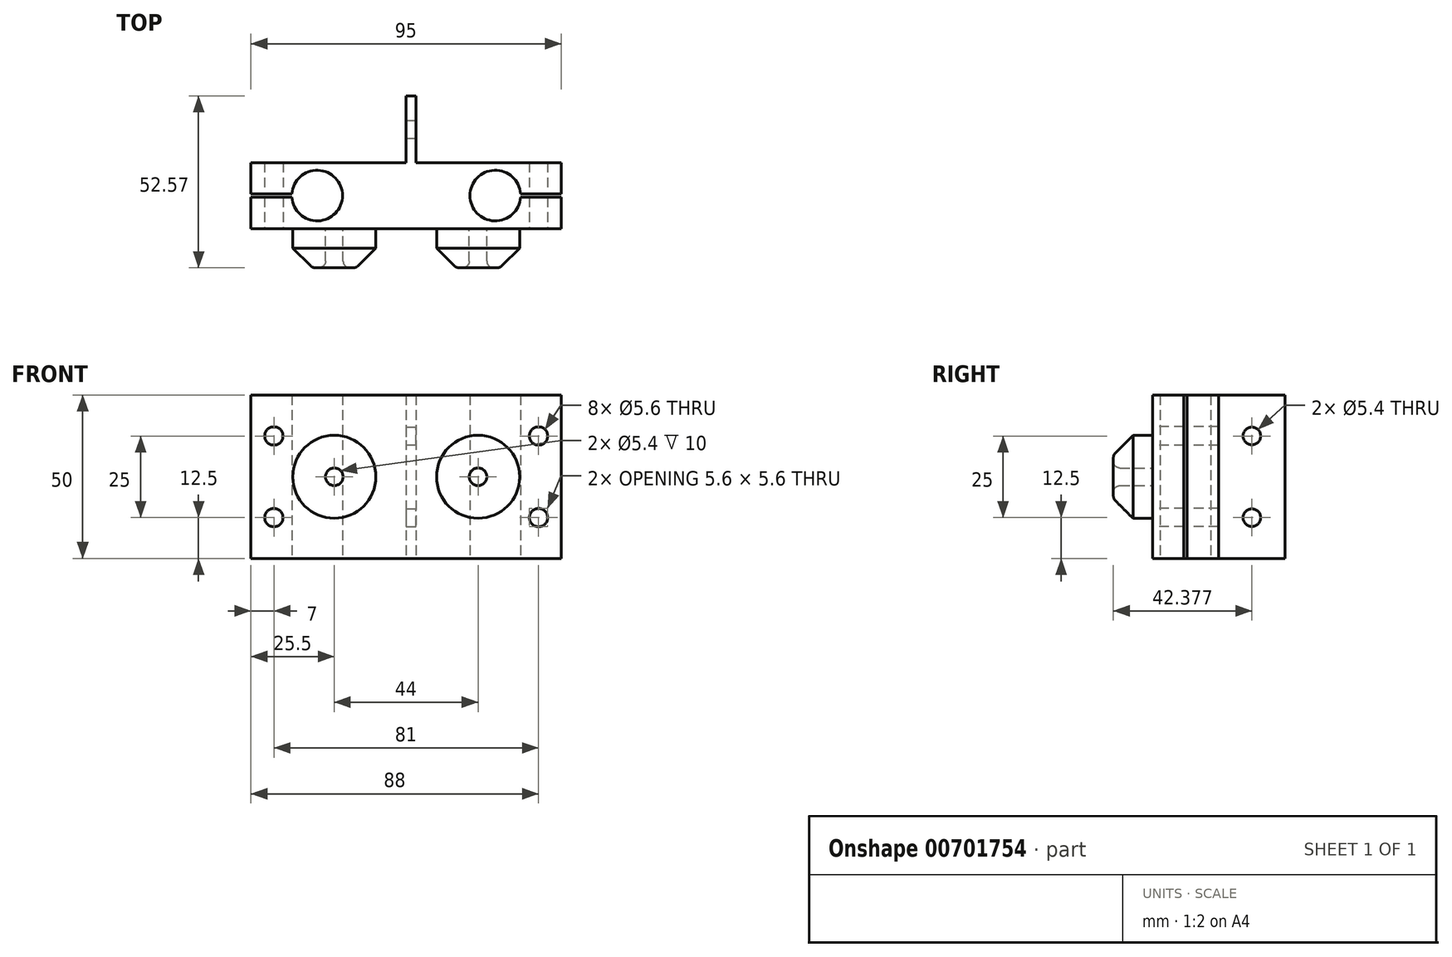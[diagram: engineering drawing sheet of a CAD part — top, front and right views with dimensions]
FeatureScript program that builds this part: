
annotation { "Feature Type Name" : "Feature", "Feature Type Description" : "" }
export const myFeature = defineFeature(function(context is Context, id is Id, definition is map)
    precondition{}
    {
        {
            var Q0;
            Q0=qCreatedBy(makeId("Top.planeOp"),FACE);
            var sketch = newSketch(context, id + "F0", { "sketchPlane" : qUnion([Q0])});
            skCircle(sketch, "E0", {"center": v(-27.25, 0) * mm, "radius": 7.75 * mm});
            skCircle(sketch, "E1", {"center": v(27.25, 0) * mm, "radius": 7.75 * mm});
            skLineSegment(sketch, "E2.bottom", {"start": v(47.5, 10.1) * mm, "end": v(-47.5, 10.1) * mm});
            skLineSegment(sketch, "E2.top", {"start": v(47.5, -10.1) * mm, "end": v(-47.5, -10.1) * mm});
            skLineSegment(sketch, "E2.left", {"start": v(47.5, 10.1) * mm, "end": v(47.5, 0.5) * mm});
            skLineSegment(sketch, "E2.right", {"start": v(-47.5, 10.1) * mm, "end": v(-47.5, 0.5) * mm});
            skPoint(sketch, "E2.middle", {"position": v(0, 0) * mm});
            skLineSegment(sketch, "E3", {"start": v(0, 10.1) * mm, "end": v(0, 36.66) * mm, "construction": true});
            skLineSegment(sketch, "E4.bottom", {"start": v(0, 10.1) * mm, "end": v(-3, 10.1) * mm});
            skLineSegment(sketch, "E4.top", {"start": v(0, 30.48) * mm, "end": v(-3, 30.48) * mm});
            skLineSegment(sketch, "E4.left", {"start": v(0, 10.1) * mm, "end": v(0, 30.48) * mm});
            skLineSegment(sketch, "E4.right", {"start": v(-3, 10.1) * mm, "end": v(-3, 30.48) * mm});
            skLineSegment(sketch, "E5.bottom", {"start": v(-4.5, 10.1) * mm, "end": v(-9.5, 10.1) * mm});
            skLineSegment(sketch, "E5.top", {"start": v(-4.5, 30.48) * mm, "end": v(-9.5, 30.48) * mm});
            skLineSegment(sketch, "E5.left", {"start": v(-4.5, 10.1) * mm, "end": v(-4.5, 30.48) * mm});
            skLineSegment(sketch, "E5.right", {"start": v(-9.5, 10.1) * mm, "end": v(-9.5, 30.48) * mm});
            skLineSegment(sketch, "E6.MirrorCS", {"start": v(0, 30.48) * mm, "end": v(3, 30.48) * mm});
            skLineSegment(sketch, "E7.MirrorCS", {"start": v(3, 10.1) * mm, "end": v(3, 30.48) * mm});
            skLineSegment(sketch, "E8.MirrorCS", {"start": v(4.5, 30.48) * mm, "end": v(9.5, 30.48) * mm});
            skLineSegment(sketch, "E9.MirrorCS", {"start": v(4.5, 10.1) * mm, "end": v(4.5, 30.48) * mm});
            skLineSegment(sketch, "E10.MirrorCS", {"start": v(9.5, 10.1) * mm, "end": v(9.5, 30.48) * mm});
            skLineSegment(sketch, "E11.bottom", {"start": v(34.98, 0.5) * mm, "end": v(47.5, 0.5) * mm});
            skLineSegment(sketch, "E11.top", {"start": v(34.98, -0.5) * mm, "end": v(47.5, -0.5) * mm});
            skLineSegment(sketch, "E11.left", {"start": v(34.98, 0.5) * mm, "end": v(34.98, -0.5) * mm});
            skLineSegment(sketch, "E12", {"start": v(47.5, 0) * mm, "end": v(35, 0) * mm, "construction": true});
            skLineSegment(sketch, "E13.MirrorCS", {"start": v(-34.98, -0.5) * mm, "end": v(-47.5, -0.5) * mm});
            skLineSegment(sketch, "E14.MirrorCS", {"start": v(-34.98, 0.5) * mm, "end": v(-47.5, 0.5) * mm});
            skLineSegment(sketch, "E15.trimOffspring", {"start": v(-47.5, -0.5) * mm, "end": v(-47.5, -10.1) * mm});
            skLineSegment(sketch, "E16.trimOffspring", {"start": v(47.5, -0.5) * mm, "end": v(47.5, -10.1) * mm});
            skSolve(sketch);
        }
        {
            var Q0;
            Q0=makeQuery(id+"F0.imprint","IMPRINT",FACE,{"disambiguationData":[TD([[makeQuery(id+"F0.imprint","IMPRINT",EDGE,{"derivedFrom":sQuery(id+"F0.wireOp",EDGE,"E0")}),-1.0]])]});
            var Q1;
            Q1=makeQuery(id+"F0.imprint","IMPRINT",FACE,{"disambiguationData":[TD([[makeQuery(id+"F0.imprint","IMPRINT",EDGE,{"derivedFrom":sQuery(id+"F0.wireOp",EDGE,"E5.bottom")}),-1.0]])]});
            var Q2;
            Q2=makeQuery(id+"F0.imprint","IMPRINT",FACE,{"disambiguationData":[TD([[makeQuery(id+"F0.imprint","IMPRINT",EDGE,{"derivedFrom":sQuery(id+"F0.wireOp",EDGE,"E4.bottom")}),-1.0]])]});
            var Q3;
            {var subQ0=sQuery(id+"F0.wireOp",EDGE,"E4.left");Q3=makeQuery(id+"F0.imprint","IMPRINT",FACE,{"disambiguationData":[TD([[makeQuery(id+"F0.imprint","IMPRINT",EDGE,{"derivedFrom":subQ0}),-1.0]])]});}
            extrude(context, id + "F1", {"entities" : qUnion([Q0, Q1, Q2, Q3]), "depth" : 50 * mm, "offsetDistance" : 25 * mm});
        }
        {
            var Q0;
            Q0=makeQuery(id+"F1.opExtrude","SWEPT_FACE",FACE,{"disambiguationData":[OSD([sQuery(id+"F0.wireOp",EDGE,"E7.MirrorCS")])]});
            var sketch = newSketch(context, id + "F2", { "sketchPlane" : qUnion([Q0])});
            skLineSegment(sketch, "E17", {"start": v(20.29, 0) * mm, "end": v(20.29, 25) * mm, "construction": true});
            skPoint(sketch, "E17.endSnap0", {"position": v(30.48, 25) * mm});
            skLineSegment(sketch, "E18", {"start": v(20.29, 25) * mm, "end": v(20.29, 50) * mm, "construction": true});
            skCircle(sketch, "E19", {"center": v(20.29, 37.5) * mm, "radius": 2.7 * mm});
            skCircle(sketch, "E20", {"center": v(20.29, 12.5) * mm, "radius": 2.7 * mm});
            skSolve(sketch);
        }
        {
            var Q0;
            Q0=makeQuery(id+"F2.imprint","IMPRINT",FACE,{"disambiguationData":[TD([[makeQuery(id+"F2.imprint","IMPRINT",EDGE,{"derivedFrom":sQuery(id+"F2.wireOp",EDGE,"E19")}),1.0]])]});
            var Q1;
            Q1=makeQuery(id+"F2.imprint","IMPRINT",FACE,{"disambiguationData":[TD([[makeQuery(id+"F2.imprint","IMPRINT",EDGE,{"derivedFrom":sQuery(id+"F2.wireOp",EDGE,"E20")}),1.0]])]});
            extrude(context, id + "F3", {"entities" : qUnion([Q0, Q1]), "operationType" : NewBodyOperationType.REMOVE, "oppositeDirection" : true, "depth" : 25 * mm, "offsetDistance" : 25 * mm});
        }
        {
            var Q0;
            Q0=makeQuery(id+"F1.opExtrude","SWEPT_FACE",FACE,{"disambiguationData":[OSD([sQuery(id+"F0.wireOp",EDGE,"E2.top")])]});
            var sketch = newSketch(context, id + "F4", { "sketchPlane" : qUnion([Q0])});
            skLineSegment(sketch, "E21", {"start": v(0, 25) * mm, "end": v(-47.5, 25) * mm, "construction": true});
            skPoint(sketch, "E21.startSnap0", {"position": v(0, 0) * mm});
            skPoint(sketch, "E21.startSnap1", {"position": v(-47.5, 25) * mm});
            skLineSegment(sketch, "E22", {"start": v(0, 25) * mm, "end": v(47.5, 25) * mm, "construction": true});
            skCircle(sketch, "E23", {"center": v(22, 25) * mm, "radius": 12.7 * mm});
            skCircle(sketch, "E24", {"center": v(-22, 25) * mm, "radius": 2.7 * mm});
            skCircle(sketch, "E25.0", {"center": v(-22, 25) * mm, "radius": 12.7 * mm});
            skCircle(sketch, "E26.0", {"center": v(22, 25) * mm, "radius": 2.7 * mm});
            skLineSegment(sketch, "E27", {"start": v(-47.5, 50) * mm, "end": v(-47.5, 25) * mm, "construction": true});
            skLineSegment(sketch, "E28", {"start": v(-47.5, 25) * mm, "end": v(-47.5, 25) * mm});
            skCircle(sketch, "E29", {"center": v(-40.5, 37.5) * mm, "radius": 2.8 * mm});
            skPoint(sketch, "E29.centerSnap0", {"position": v(-47.5, 37.5) * mm});
            skCircle(sketch, "E30.0.1.0", {"center": v(-40.5, 12.5) * mm, "radius": 2.8 * mm});
            skCircle(sketch, "E30.1.0.0", {"center": v(40.5, 37.5) * mm, "radius": 2.8 * mm});
            skCircle(sketch, "E30.1.1.0", {"center": v(40.5, 12.5) * mm, "radius": 2.8 * mm});
            skLineSegment(sketch, "E30.direction1", {"start": v(-40.5, 37.5) * mm, "end": v(40.5, 37.5) * mm, "construction": true});
            skLineSegment(sketch, "E30.direction2", {"start": v(-40.5, 37.5) * mm, "end": v(-40.5, 12.5) * mm, "construction": true});
            skSolve(sketch);
        }
        {
            var Q0;
            Q0=makeQuery(id+"F4.imprint","IMPRINT",FACE,{"disambiguationData":[TD([[makeQuery(id+"F4.imprint","IMPRINT",EDGE,{"derivedFrom":sQuery(id+"F4.wireOp",EDGE,"E24")}),-1.0]])]});
            var Q1;
            Q1=makeQuery(id+"F4.imprint","IMPRINT",FACE,{"disambiguationData":[TD([[makeQuery(id+"F4.imprint","IMPRINT",EDGE,{"derivedFrom":sQuery(id+"F4.wireOp",EDGE,"E23")}),1.0]])]});
            extrude(context, id + "F5", {"entities" : qUnion([Q0, Q1]), "operationType" : NewBodyOperationType.ADD, "depth" : 12 * mm, "offsetDistance" : 25 * mm});
        }
        {
            var Q0;
            Q0=makeQuery(id+"F5.opExtrude","CAP_EDGE",EDGE,{"disambiguationData":[OSD([sQuery(id+"F4.wireOp",EDGE,"E25.0")])],"isStart":true});
            var Q1;
            Q1=makeQuery(id+"F5.opExtrude","CAP_EDGE",EDGE,{"disambiguationData":[OSD([sQuery(id+"F4.wireOp",EDGE,"E25.0")])],"isStart":false});
            var Q2;
            Q2=makeQuery(id+"F5.opExtrude","CAP_EDGE",EDGE,{"disambiguationData":[OSD([sQuery(id+"F4.wireOp",EDGE,"E23")])],"isStart":false});
            var Q3;
            Q3=makeQuery(id+"F5.opExtrude","CAP_EDGE",EDGE,{"disambiguationData":[OSD([sQuery(id+"F4.wireOp",EDGE,"E23")])],"isStart":true});
            chamfer(context, id + "F6", {"entities" : qUnion([Q0, Q1, Q2, Q3]), "width" : 6 * mm, "tangentPropagation" : true});
        }
        {
            var Q0;
            Q0=makeQuery(id+"F4.imprint","IMPRINT",FACE,{"disambiguationData":[TD([[makeQuery(id+"F4.imprint","IMPRINT",EDGE,{"derivedFrom":sQuery(id+"F4.wireOp",EDGE,"E29")}),1.0]])]});
            var Q1;
            Q1=makeQuery(id+"F4.imprint","IMPRINT",FACE,{"disambiguationData":[TD([[makeQuery(id+"F4.imprint","IMPRINT",EDGE,{"derivedFrom":sQuery(id+"F4.wireOp",EDGE,"E30.0.1.0")}),1.0]])]});
            var Q2;
            Q2=makeQuery(id+"F4.imprint","IMPRINT",FACE,{"disambiguationData":[TD([[makeQuery(id+"F4.imprint","IMPRINT",EDGE,{"derivedFrom":sQuery(id+"F4.wireOp",EDGE,"E30.1.0.0")}),1.0]])]});
            var Q3;
            Q3=makeQuery(id+"F4.imprint","IMPRINT",FACE,{"disambiguationData":[TD([[makeQuery(id+"F4.imprint","IMPRINT",EDGE,{"derivedFrom":sQuery(id+"F4.wireOp",EDGE,"E30.1.1.0")}),1.0]])]});
            extrude(context, id + "F7", {"entities" : qUnion([Q0, Q1, Q2, Q3]), "operationType" : NewBodyOperationType.REMOVE, "oppositeDirection" : true, "depth" : 25 * mm, "offsetDistance" : 25 * mm});
        }
        {
            var Q0;
            Q0=makeQuery(id+"F5.opExtrude","CAP_FACE",FACE,{"disambiguationData":[OSD([sQuery(id+"F4.wireOp",EDGE,"E24"),sQuery(id+"F4.wireOp",EDGE,"E25.0")])],"isStart":false});
            var Q1;
            Q1=makeQuery(id+"F5.opExtrude","CAP_FACE",FACE,{"disambiguationData":[OSD([sQuery(id+"F4.wireOp",EDGE,"E23"),sQuery(id+"F4.wireOp",EDGE,"E26.0")])],"isStart":false});
            fillet(context, id + "F8", {"entities" : qUnion([Q0, Q1]), "radius" : 2 * mm, "tangentPropagation" : true, "allowEdgeOverflow" : false});
        }
    });
